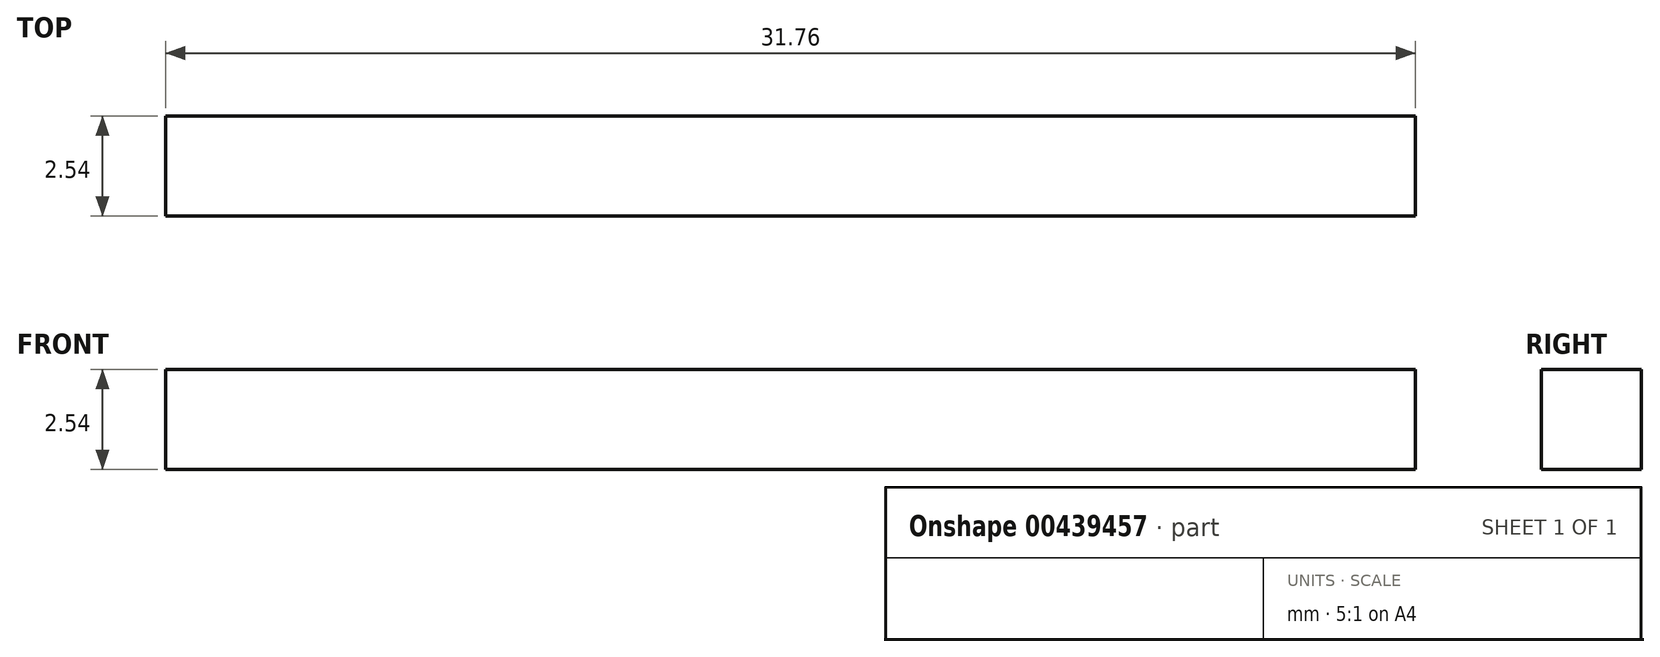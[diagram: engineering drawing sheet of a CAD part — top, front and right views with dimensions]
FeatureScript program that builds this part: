
annotation { "Feature Type Name" : "Feature", "Feature Type Description" : "" }
export const myFeature = defineFeature(function(context is Context, id is Id, definition is map)
    precondition{}
    {
        {
            var Q0;
            Q0=qCreatedBy(makeId("Front.planeOp"),FACE);
            var sketch = newSketch(context, id + "F0", { "sketchPlane" : qUnion([Q0])});
            skLineSegment(sketch, "E0.bottom", {"start": v(-15.88, 0) * mm, "end": v(15.88, 0) * mm});
            skLineSegment(sketch, "E0.top", {"start": v(-15.88, 2.54) * mm, "end": v(15.88, 2.54) * mm});
            skLineSegment(sketch, "E0.left", {"start": v(-15.88, 0) * mm, "end": v(-15.88, 2.54) * mm});
            skLineSegment(sketch, "E0.right", {"start": v(15.88, 0) * mm, "end": v(15.88, 2.54) * mm});
            skSolve(sketch);
        }
        {
            var Q0;
            Q0=makeQuery(id+"F0.imprint","IMPRINT",FACE,{"disambiguationData":[TD([[makeQuery(id+"F0.imprint","IMPRINT",EDGE,{"derivedFrom":sQuery(id+"F0.wireOp",EDGE,"E0.bottom")}),1.0]])]});
            extrude(context, id + "F1", {"entities" : qUnion([Q0]), "depth" : 2.54 * mm});
        }
    });
